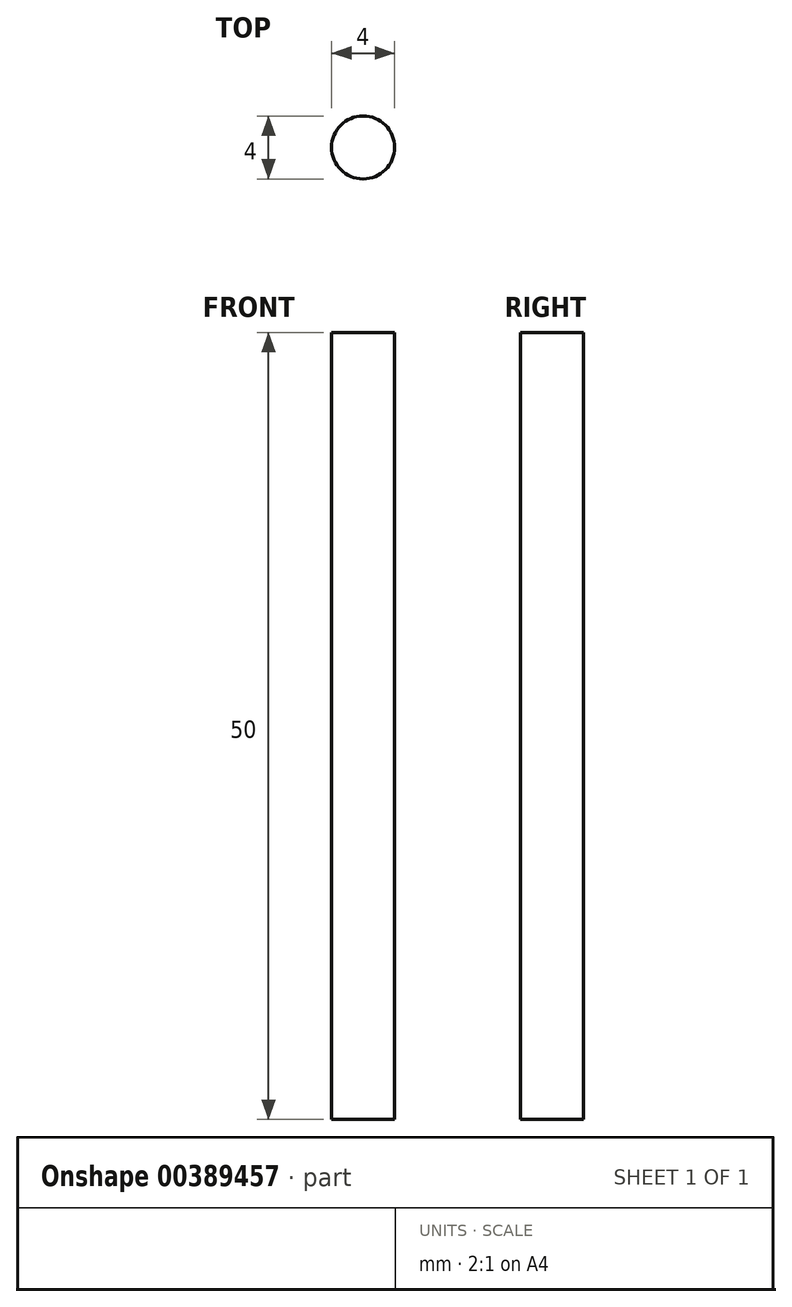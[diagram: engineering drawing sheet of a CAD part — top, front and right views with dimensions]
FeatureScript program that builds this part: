
annotation { "Feature Type Name" : "Feature", "Feature Type Description" : "" }
export const myFeature = defineFeature(function(context is Context, id is Id, definition is map)
    precondition{}
    {
        {
            var Q0;
            Q0=qCreatedBy(makeId("Top.planeOp"),FACE);
            var sketch = newSketch(context, id + "F0", { "sketchPlane" : qUnion([Q0])});
            skCircle(sketch, "E0", {"center": v(0, 0) * mm, "radius": 2 * mm});
            skSolve(sketch);
        }
        {
            var Q0;
            Q0=qSketchRegion(id+"F0",true);
            extrude(context, id + "F1", {"entities" : qUnion([Q0]), "endBound" : BoundingType.SYMMETRIC, "depth" : 50 * mm});
        }
    });
